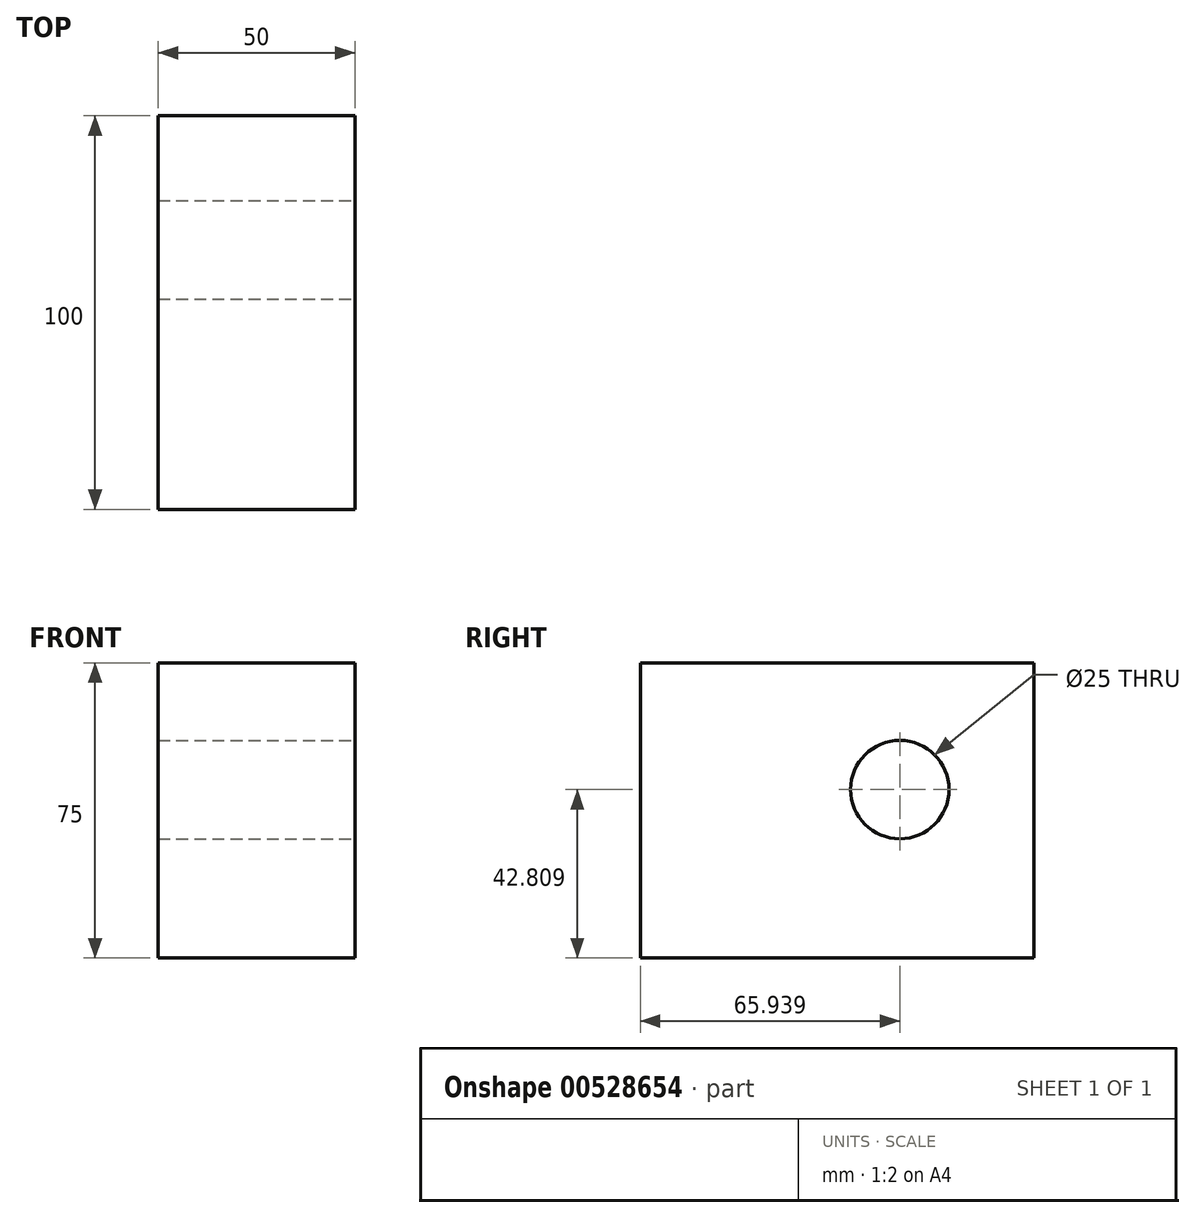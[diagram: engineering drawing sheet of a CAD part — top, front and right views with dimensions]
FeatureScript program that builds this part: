
annotation { "Feature Type Name" : "Feature", "Feature Type Description" : "" }
export const myFeature = defineFeature(function(context is Context, id is Id, definition is map)
    precondition{}
    {
        {
            var Q0;
            Q0=qCreatedBy(makeId("Front.planeOp"),FACE);
            var sketch = newSketch(context, id + "F0", { "sketchPlane" : qUnion([Q0])});
            skLineSegment(sketch, "E0.bottom", {"start": v(-36.86, 72.53) * mm, "end": v(13.14, 72.53) * mm});
            skLineSegment(sketch, "E0.top", {"start": v(-36.86, -2.47) * mm, "end": v(13.14, -2.47) * mm});
            skLineSegment(sketch, "E0.left", {"start": v(-36.86, 72.53) * mm, "end": v(-36.86, -2.47) * mm});
            skLineSegment(sketch, "E0.right", {"start": v(13.14, 72.53) * mm, "end": v(13.14, -2.47) * mm});
            skSolve(sketch);
        }
        {
            var Q0;
            Q0 = qSketchRegion(id + "F0", true);
            extrude(context, id + "F1", {"entities" : qUnion([Q0]), "endBound" : BoundingType.SYMMETRIC, "depth" : 100 * mm, "offsetDistance" : 25 * mm});
        }
        {
            var Q0;
            Q0=makeQuery(id+"F1.opExtrude","SWEPT_FACE",FACE,{"disambiguationData":[OSD([sQuery(id+"F0.wireOp",EDGE,"E0.right")])]});
            var sketch = newSketch(context, id + "F2", { "sketchPlane" : qUnion([Q0])});
            skPoint(sketch, "E1", {"position": v(15.94, 40.34) * mm});
            skSolve(sketch);
        }
        {
            var Q0;
            Q0=sQuery(id+"F2.wireOp",VERTEX,"E1");
            var Q1;
            Q1=makeQuery(id+"F1.opExtrude","SWEPT_BODY",BODY,{"disambiguationData":[OSD([sQuery(id+"F0.wireOp",EDGE,"E0.bottom"),sQuery(id+"F0.wireOp",EDGE,"E0.top"),sQuery(id+"F0.wireOp",EDGE,"E0.left"),sQuery(id+"F0.wireOp",EDGE,"E0.right")])]});
            hole(context, id + "F3", {"style" : HoleStyle.SIMPLE, "endStyle" : HoleEndStyle.THROUGH, "holeDiameter" : 25 * mm, "isTappedThrough" : true, "tappedDepth" : 12 * mm, "tapClearance" : 3, "locations" : qUnion([Q0]), "scope" : qUnion([Q1])});
        }
    });
